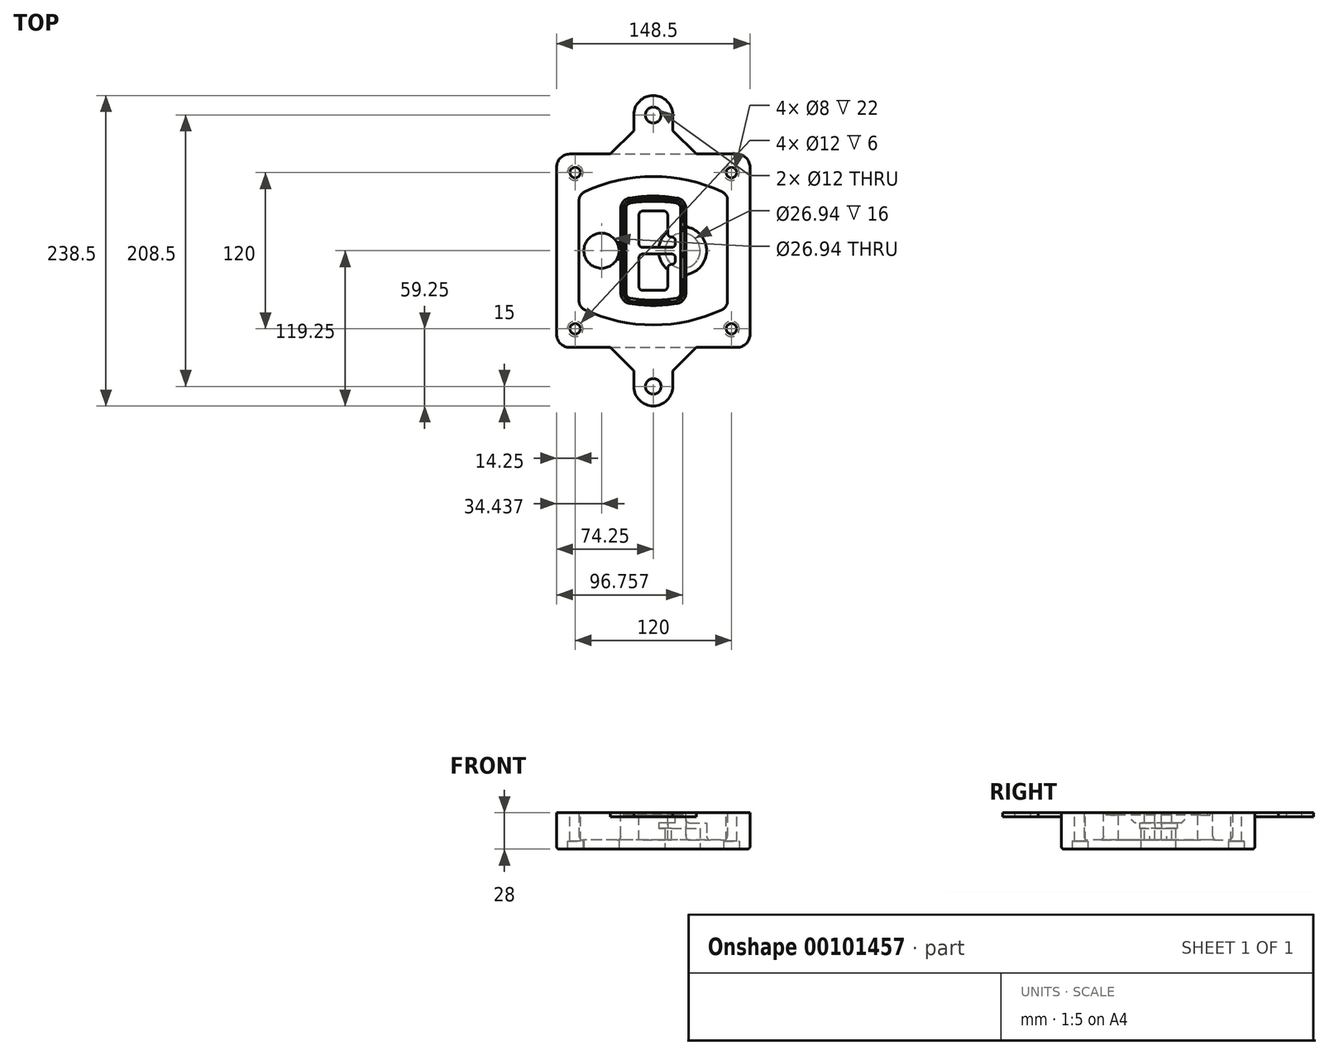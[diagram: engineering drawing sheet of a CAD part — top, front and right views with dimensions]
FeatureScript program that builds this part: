
annotation { "Feature Type Name" : "Feature", "Feature Type Description" : "" }
export const myFeature = defineFeature(function(context is Context, id is Id, definition is map)
    precondition{}
    {
        {
            var Q0;
            Q0=qCreatedBy(makeId("Top.planeOp"),FACE);
            var sketch = newSketch(context, id + "F0", { "sketchPlane" : qUnion([Q0])});
            skPoint(sketch, "E0.rect.middle", {"position": v(0, 0) * mm});
            skLineSegment(sketch, "E1.bottom", {"start": v(-64.25, -74.25) * mm, "end": v(64.25, -74.25) * mm});
            skLineSegment(sketch, "E1.top", {"start": v(-64.25, 74.25) * mm, "end": v(64.25, 74.25) * mm});
            skLineSegment(sketch, "E1.left", {"start": v(-74.25, -64.25) * mm, "end": v(-74.25, 64.25) * mm});
            skLineSegment(sketch, "E1.right", {"start": v(74.25, -64.25) * mm, "end": v(74.25, 64.25) * mm});
            skLineSegment(sketch, "E2", {"start": v(-74.25, 74.25) * mm, "end": v(74.25, -74.25) * mm, "construction": true});
            skLineSegment(sketch, "E3", {"start": v(74.25, 74.25) * mm, "end": v(-74.25, -74.25) * mm, "construction": true});
            skCircle(sketch, "E4", {"center": v(-60, 60) * mm, "radius": 4 * mm});
            skCircle(sketch, "E5", {"center": v(60, 60) * mm, "radius": 4 * mm});
            skCircle(sketch, "E6", {"center": v(60, -60) * mm, "radius": 4 * mm});
            skCircle(sketch, "E7", {"center": v(-60, -60) * mm, "radius": 4 * mm});
            skLineSegment(sketch, "E8", {"start": v(-60, 60) * mm, "end": v(60, 60) * mm, "construction": true});
            skLineSegment(sketch, "E9", {"start": v(60, 60) * mm, "end": v(60, -60) * mm, "construction": true});
            skLineSegment(sketch, "E10", {"start": v(60, -60) * mm, "end": v(-60, -60) * mm, "construction": true});
            skLineSegment(sketch, "E11", {"start": v(-60, -60) * mm, "end": v(-60, 60) * mm, "construction": true});
            skLineSegment(sketch, "E12", {"start": v(-60, 38.83) * mm, "end": v(-60, -38.83) * mm});
            skLineSegment(sketch, "E13", {"start": v(60, 38.83) * mm, "end": v(60, -38.83) * mm});
            skArc(sketch, "E14", {"start": v(54.26, 47.88) * mm, "mid": v(0, 60) * mm, "end": v(-54.26, 47.88) * mm});
            skArc(sketch, "E15", {"start": v(-54.26, -47.88) * mm, "mid": v(0, -60) * mm, "end": v(54.26, -47.88) * mm});
            skLineSegment(sketch, "E16", {"start": v(-60, 0) * mm, "end": v(60, 0) * mm, "construction": true});
            skPoint(sketch, "E17.visualSharp", {"position": v(-60, -45) * mm});
            skArc(sketch, "E17.filletArc", {"start": v(-60, -38.83) * mm, "mid": v(-58.44, -44.2) * mm, "end": v(-54.26, -47.88) * mm});
            skPoint(sketch, "E18.visualSharp", {"position": v(-60, 45) * mm});
            skArc(sketch, "E18.filletArc", {"start": v(-54.26, 47.88) * mm, "mid": v(-58.44, 44.2) * mm, "end": v(-60, 38.83) * mm});
            skPoint(sketch, "E19.visualSharp", {"position": v(60, 45) * mm});
            skArc(sketch, "E19.filletArc", {"start": v(60, 38.83) * mm, "mid": v(58.44, 44.2) * mm, "end": v(54.26, 47.88) * mm});
            skPoint(sketch, "E20.visualSharp", {"position": v(60, -45) * mm});
            skArc(sketch, "E20.filletArc", {"start": v(54.26, -47.88) * mm, "mid": v(58.44, -44.2) * mm, "end": v(60, -38.83) * mm});
            skPoint(sketch, "E21.visualSharp", {"position": v(-74.25, 74.25) * mm});
            skArc(sketch, "E21.filletArc", {"start": v(-64.25, 74.25) * mm, "mid": v(-71.32, 71.32) * mm, "end": v(-74.25, 64.25) * mm});
            skPoint(sketch, "E22.visualSharp", {"position": v(74.25, 74.25) * mm});
            skArc(sketch, "E22.filletArc", {"start": v(74.25, 64.25) * mm, "mid": v(71.32, 71.32) * mm, "end": v(64.25, 74.25) * mm});
            skPoint(sketch, "E23.visualSharp", {"position": v(74.25, -74.25) * mm});
            skArc(sketch, "E23.filletArc", {"start": v(64.25, -74.25) * mm, "mid": v(71.32, -71.32) * mm, "end": v(74.25, -64.25) * mm});
            skPoint(sketch, "E24.visualSharp", {"position": v(-74.25, -74.25) * mm});
            skArc(sketch, "E24.filletArc", {"start": v(-74.25, -64.25) * mm, "mid": v(-71.32, -71.32) * mm, "end": v(-64.25, -74.25) * mm});
            skArc(sketch, "E25.0", {"start": v(57, 38.83) * mm, "mid": v(55.9, 42.58) * mm, "end": v(52.98, 45.17) * mm});
            skLineSegment(sketch, "E25.1", {"start": v(57, 38.83) * mm, "end": v(57, -38.83) * mm});
            skArc(sketch, "E25.2", {"start": v(52.98, -45.17) * mm, "mid": v(55.9, -42.58) * mm, "end": v(57, -38.83) * mm});
            skArc(sketch, "E25.3", {"start": v(-52.98, -45.17) * mm, "mid": v(0, -57) * mm, "end": v(52.98, -45.17) * mm});
            skArc(sketch, "E25.4", {"start": v(-57, -38.83) * mm, "mid": v(-55.9, -42.58) * mm, "end": v(-52.98, -45.17) * mm});
            skArc(sketch, "E25.5", {"start": v(52.98, 45.17) * mm, "mid": v(0, 57) * mm, "end": v(-52.98, 45.17) * mm});
            skLineSegment(sketch, "E25.6", {"start": v(-57, 38.83) * mm, "end": v(-57, -38.83) * mm});
            skArc(sketch, "E25.7", {"start": v(-52.98, 45.17) * mm, "mid": v(-55.9, 42.58) * mm, "end": v(-57, 38.83) * mm});
            skArc(sketch, "E26.0", {"start": v(-55.96, 51.5) * mm, "mid": v(-61.82, 46.33) * mm, "end": v(-64, 38.83) * mm});
            skArc(sketch, "E26.1", {"start": v(55.96, 51.5) * mm, "mid": v(0, 64) * mm, "end": v(-55.96, 51.5) * mm});
            skArc(sketch, "E26.2", {"start": v(64, 38.83) * mm, "mid": v(61.82, 46.33) * mm, "end": v(55.96, 51.5) * mm});
            skLineSegment(sketch, "E26.3", {"start": v(64, 38.83) * mm, "end": v(64, -38.83) * mm});
            skArc(sketch, "E26.4", {"start": v(55.96, -51.5) * mm, "mid": v(61.82, -46.33) * mm, "end": v(64, -38.83) * mm});
            skLineSegment(sketch, "E26.5", {"start": v(-64, 38.83) * mm, "end": v(-64, -38.83) * mm});
            skArc(sketch, "E26.6", {"start": v(-55.96, -51.5) * mm, "mid": v(0, -64) * mm, "end": v(55.96, -51.5) * mm});
            skArc(sketch, "E26.7", {"start": v(-64, -38.83) * mm, "mid": v(-61.82, -46.33) * mm, "end": v(-55.96, -51.5) * mm});
            skSolve(sketch);
        }
        {
            var Q0;
            Q0=makeQuery(id+"F0.imprint","IMPRINT",FACE,{"disambiguationData":[TD([[makeQuery(id+"F0.imprint","IMPRINT",EDGE,{"derivedFrom":sQuery(id+"F0.wireOp",EDGE,"E1.bottom")}),1.0]])]});
            var Q1;
            Q1=makeQuery(id+"F0.imprint","IMPRINT",FACE,{"disambiguationData":[TD([[makeQuery(id+"F0.imprint","IMPRINT",EDGE,{"derivedFrom":sQuery(id+"F0.wireOp",EDGE,"E12")}),1.0]])]});
            var Q2;
            Q2=makeQuery(id+"F0.imprint","IMPRINT",FACE,{"disambiguationData":[TD([[makeQuery(id+"F0.imprint","IMPRINT",EDGE,{"derivedFrom":sQuery(id+"F0.wireOp",EDGE,"E25.0")}),1.0]])]});
            var Q3;
            Q3=makeQuery(id+"F0.imprint","IMPRINT",FACE,{"disambiguationData":[TD([[makeQuery(id+"F0.imprint","IMPRINT",EDGE,{"derivedFrom":sQuery(id+"F0.wireOp",EDGE,"E12")}),-1.0]])]});
            extrude(context, id + "F1", {"entities" : qUnion([Q0, Q1, Q2, Q3]), "oppositeDirection" : true, "depth" : 25 * mm});
        }
        {
            var Q0;
            Q0=makeQuery(id+"F0.imprint","IMPRINT",FACE,{"disambiguationData":[TD([[makeQuery(id+"F0.imprint","IMPRINT",EDGE,{"derivedFrom":sQuery(id+"F0.wireOp",EDGE,"E12")}),1.0]])]});
            extrude(context, id + "F2", {"entities" : qUnion([Q0]), "operationType" : NewBodyOperationType.ADD, "depth" : 3 * mm});
        }
        {
            var Q0;
            Q0=makeQuery(id+"F0.imprint","IMPRINT",FACE,{"disambiguationData":[TD([[makeQuery(id+"F0.imprint","IMPRINT",EDGE,{"derivedFrom":sQuery(id+"F0.wireOp",EDGE,"E25.0")}),1.0]])]});
            extrude(context, id + "F3", {"entities" : qUnion([Q0]), "operationType" : NewBodyOperationType.REMOVE, "oppositeDirection" : true, "depth" : 18 * mm});
        }
        {
            var Q0;
            Q0=makeQuery(id+"F2.opExtrude","CAP_FACE",FACE,{"disambiguationData":[OSD([sQuery(id+"F0.wireOp",EDGE,"E12"),sQuery(id+"F0.wireOp",EDGE,"E13"),sQuery(id+"F0.wireOp",EDGE,"E14"),sQuery(id+"F0.wireOp",EDGE,"E15"),sQuery(id+"F0.wireOp",EDGE,"E17.filletArc"),sQuery(id+"F0.wireOp",EDGE,"E18.filletArc"),sQuery(id+"F0.wireOp",EDGE,"E19.filletArc"),sQuery(id+"F0.wireOp",EDGE,"E20.filletArc"),sQuery(id+"F0.wireOp",EDGE,"E25.0"),sQuery(id+"F0.wireOp",EDGE,"E25.1"),sQuery(id+"F0.wireOp",EDGE,"E25.2"),sQuery(id+"F0.wireOp",EDGE,"E25.3"),sQuery(id+"F0.wireOp",EDGE,"E25.4"),sQuery(id+"F0.wireOp",EDGE,"E25.5"),sQuery(id+"F0.wireOp",EDGE,"E25.6"),sQuery(id+"F0.wireOp",EDGE,"E25.7")])],"isStart":false});
            var sketch = newSketch(context, id + "F4", { "sketchPlane" : qUnion([Q0])});
            skArc(sketch, "E27.0", {"start": v(-18.34, -40.45) * mm, "mid": v(0, -42) * mm, "end": v(18.34, -40.45) * mm});
            skArc(sketch, "E28.0", {"start": v(18.34, 40.45) * mm, "mid": v(0, 42) * mm, "end": v(-18.34, 40.45) * mm});
            skLineSegment(sketch, "E29", {"start": v(-25, 32.57) * mm, "end": v(-25, -32.57) * mm});
            skLineSegment(sketch, "E30", {"start": v(25, 32.57) * mm, "end": v(25, -32.57) * mm});
            skLineSegment(sketch, "E31", {"start": v(-25, 39.1) * mm, "end": v(25, 39.1) * mm, "construction": true});
            skLineSegment(sketch, "E32", {"start": v(-25, -39.1) * mm, "end": v(25, -39.1) * mm, "construction": true});
            skPoint(sketch, "E33.visualSharp", {"position": v(-25, 39.1) * mm});
            skArc(sketch, "E33.filletArc", {"start": v(-18.34, 40.45) * mm, "mid": v(-23.11, 37.73) * mm, "end": v(-25, 32.57) * mm});
            skPoint(sketch, "E34.visualSharp", {"position": v(25, 39.1) * mm});
            skArc(sketch, "E34.filletArc", {"start": v(25, 32.57) * mm, "mid": v(23.11, 37.73) * mm, "end": v(18.34, 40.45) * mm});
            skPoint(sketch, "E35.visualSharp", {"position": v(25, -39.1) * mm});
            skArc(sketch, "E35.filletArc", {"start": v(18.34, -40.45) * mm, "mid": v(23.11, -37.73) * mm, "end": v(25, -32.57) * mm});
            skPoint(sketch, "E36.visualSharp", {"position": v(-25, -39.1) * mm});
            skArc(sketch, "E36.filletArc", {"start": v(-25, -32.57) * mm, "mid": v(-23.11, -37.73) * mm, "end": v(-18.34, -40.45) * mm});
            skArc(sketch, "E37.0", {"start": v(52.98, 45.17) * mm, "mid": v(0, 57) * mm, "end": v(-52.98, 45.17) * mm});
            skArc(sketch, "E37.1", {"start": v(-52.98, 45.17) * mm, "mid": v(-55.9, 42.58) * mm, "end": v(-57, 38.83) * mm});
            skLineSegment(sketch, "E37.2", {"start": v(-57, 38.83) * mm, "end": v(-57, -38.83) * mm});
            skArc(sketch, "E37.3", {"start": v(-57, -38.83) * mm, "mid": v(-55.9, -42.58) * mm, "end": v(-52.98, -45.17) * mm});
            skArc(sketch, "E37.4", {"start": v(-52.98, -45.17) * mm, "mid": v(0, -57) * mm, "end": v(52.98, -45.17) * mm});
            skArc(sketch, "E37.5", {"start": v(52.98, -45.17) * mm, "mid": v(55.9, -42.58) * mm, "end": v(57, -38.83) * mm});
            skLineSegment(sketch, "E37.6", {"start": v(57, 38.83) * mm, "end": v(57, -38.83) * mm});
            skArc(sketch, "E37.7", {"start": v(57, 38.83) * mm, "mid": v(55.9, 42.58) * mm, "end": v(52.98, 45.17) * mm});
            skLineSegment(sketch, "E38.0", {"start": v(23, 32.57) * mm, "end": v(23, -32.57) * mm});
            skArc(sketch, "E38.1", {"start": v(18, -38.48) * mm, "mid": v(21.58, -36.44) * mm, "end": v(23, -32.57) * mm});
            skArc(sketch, "E38.2", {"start": v(-18, -38.48) * mm, "mid": v(0, -40) * mm, "end": v(18, -38.48) * mm});
            skArc(sketch, "E38.3", {"start": v(-23, -32.57) * mm, "mid": v(-21.58, -36.44) * mm, "end": v(-18, -38.48) * mm});
            skLineSegment(sketch, "E38.4", {"start": v(-23, 32.57) * mm, "end": v(-23, -32.57) * mm});
            skArc(sketch, "E38.5", {"start": v(23, 32.57) * mm, "mid": v(21.58, 36.44) * mm, "end": v(18, 38.48) * mm});
            skArc(sketch, "E38.6", {"start": v(-18, 38.48) * mm, "mid": v(-21.58, 36.44) * mm, "end": v(-23, 32.57) * mm});
            skArc(sketch, "E38.7", {"start": v(18, 38.48) * mm, "mid": v(0, 40) * mm, "end": v(-18, 38.48) * mm});
            skArc(sketch, "E39.0", {"start": v(21, 32.57) * mm, "mid": v(20.06, 35.15) * mm, "end": v(17.67, 36.5) * mm});
            skLineSegment(sketch, "E39.1", {"start": v(21, 32.57) * mm, "end": v(21, -32.57) * mm});
            skArc(sketch, "E39.2", {"start": v(17.67, -36.5) * mm, "mid": v(20.06, -35.15) * mm, "end": v(21, -32.57) * mm});
            skArc(sketch, "E39.3", {"start": v(-17.67, -36.5) * mm, "mid": v(0, -38) * mm, "end": v(17.67, -36.5) * mm});
            skArc(sketch, "E39.4", {"start": v(-21, -32.57) * mm, "mid": v(-20.06, -35.15) * mm, "end": v(-17.67, -36.5) * mm});
            skArc(sketch, "E39.5", {"start": v(17.67, 36.5) * mm, "mid": v(0, 38) * mm, "end": v(-17.67, 36.5) * mm});
            skLineSegment(sketch, "E39.6", {"start": v(-21, 32.57) * mm, "end": v(-21, -32.57) * mm});
            skArc(sketch, "E39.7", {"start": v(-17.67, 36.5) * mm, "mid": v(-20.06, 35.15) * mm, "end": v(-21, 32.57) * mm});
            skLineSegment(sketch, "E40", {"start": v(-25, 0) * mm, "end": v(25, 0) * mm, "construction": true});
            skLineSegment(sketch, "E41", {"start": v(-11, 5.5) * mm, "end": v(-11, 27.5) * mm});
            skLineSegment(sketch, "E42", {"start": v(-8, 30.5) * mm, "end": v(8, 30.5) * mm});
            skLineSegment(sketch, "E43", {"start": v(11, 27.5) * mm, "end": v(11, 13.5) * mm});
            skLineSegment(sketch, "E44", {"start": v(14, 10.5) * mm, "end": v(14, 10.5) * mm});
            skLineSegment(sketch, "E45", {"start": v(17, 7.5) * mm, "end": v(17, 5.5) * mm});
            skLineSegment(sketch, "E46", {"start": v(14, 2.5) * mm, "end": v(-8, 2.5) * mm});
            skPoint(sketch, "E47.visualSharp", {"position": v(-11, 30.5) * mm});
            skArc(sketch, "E47.filletArc", {"start": v(-8, 30.5) * mm, "mid": v(-10.12, 29.62) * mm, "end": v(-11, 27.5) * mm});
            skPoint(sketch, "E48.visualSharp", {"position": v(11, 30.5) * mm});
            skArc(sketch, "E48.filletArc", {"start": v(11, 27.5) * mm, "mid": v(10.12, 29.62) * mm, "end": v(8, 30.5) * mm});
            skPoint(sketch, "E49.visualSharp", {"position": v(11, 10.5) * mm});
            skArc(sketch, "E49.filletArc", {"start": v(11, 13.5) * mm, "mid": v(11.88, 11.38) * mm, "end": v(14, 10.5) * mm});
            skPoint(sketch, "E50.visualSharp", {"position": v(17, 10.5) * mm});
            skArc(sketch, "E50.filletArc", {"start": v(17, 7.5) * mm, "mid": v(16.12, 9.62) * mm, "end": v(14, 10.5) * mm});
            skPoint(sketch, "E51.visualSharp", {"position": v(17, 2.5) * mm});
            skArc(sketch, "E51.filletArc", {"start": v(14, 2.5) * mm, "mid": v(16.12, 3.38) * mm, "end": v(17, 5.5) * mm});
            skPoint(sketch, "E52.visualSharp", {"position": v(-11, 2.5) * mm});
            skArc(sketch, "E52.filletArc", {"start": v(-11, 5.5) * mm, "mid": v(-10.12, 3.38) * mm, "end": v(-8, 2.5) * mm});
            skLineSegment(sketch, "E53.0.MirrorCS", {"start": v(14, -2.5) * mm, "end": v(-8, -2.5) * mm});
            skArc(sketch, "E54.0.MirrorCS", {"start": v(-11, -5.5) * mm, "mid": v(-10.12, -3.38) * mm, "end": v(-8, -2.5) * mm});
            skLineSegment(sketch, "E55.0.MirrorCS", {"start": v(-11, -5.5) * mm, "end": v(-11, -27.5) * mm});
            skArc(sketch, "E56.0.MirrorCS", {"start": v(-8, -30.5) * mm, "mid": v(-10.12, -29.62) * mm, "end": v(-11, -27.5) * mm});
            skLineSegment(sketch, "E57.0.MirrorCS", {"start": v(-8, -30.5) * mm, "end": v(8, -30.5) * mm});
            skArc(sketch, "E58.0.MirrorCS", {"start": v(11, -27.5) * mm, "mid": v(10.12, -29.62) * mm, "end": v(8, -30.5) * mm});
            skLineSegment(sketch, "E59.0.MirrorCS", {"start": v(11, -27.5) * mm, "end": v(11, -13.5) * mm});
            skArc(sketch, "E60.0.MirrorCS", {"start": v(11, -13.5) * mm, "mid": v(11.88, -11.38) * mm, "end": v(14, -10.5) * mm});
            skArc(sketch, "E61.0.MirrorCS", {"start": v(17, -7.5) * mm, "mid": v(16.12, -9.62) * mm, "end": v(14, -10.5) * mm});
            skLineSegment(sketch, "E62.0.MirrorCS", {"start": v(17, -7.5) * mm, "end": v(17, -5.5) * mm});
            skArc(sketch, "E63.0.MirrorCS", {"start": v(14, -2.5) * mm, "mid": v(16.12, -3.38) * mm, "end": v(17, -5.5) * mm});
            skSolve(sketch);
        }
        {
            var Q0;
            Q0=makeQuery(id+"F4.imprint","IMPRINT",FACE,{"disambiguationData":[TD([[makeQuery(id+"F4.imprint","IMPRINT",EDGE,{"derivedFrom":sQuery(id+"F4.wireOp",EDGE,"E27.0")}),1.0]])]});
            var Q1;
            Q1=makeQuery(id+"F4.imprint","IMPRINT",FACE,{"disambiguationData":[TD([[makeQuery(id+"F4.imprint","IMPRINT",EDGE,{"derivedFrom":sQuery(id+"F4.wireOp",EDGE,"E38.0")}),-1.0]])]});
            var Q2;
            Q2=makeQuery(id+"F4.imprint","IMPRINT",FACE,{"disambiguationData":[TD([[makeQuery(id+"F4.imprint","IMPRINT",EDGE,{"derivedFrom":sQuery(id+"F4.wireOp",EDGE,"E39.0")}),1.0]])]});
            extrude(context, id + "F5", {"entities" : qUnion([Q0, Q1, Q2]), "operationType" : NewBodyOperationType.ADD, "endBound" : BoundingType.UP_TO_NEXT, "oppositeDirection" : true, "depth" : 25 * mm});
        }
        {
            var Q0;
            Q0=makeQuery(id+"F4.imprint","IMPRINT",FACE,{"disambiguationData":[TD([[makeQuery(id+"F4.imprint","IMPRINT",EDGE,{"derivedFrom":sQuery(id+"F4.wireOp",EDGE,"E38.0")}),-1.0]])]});
            extrude(context, id + "F6", {"entities" : qUnion([Q0]), "operationType" : NewBodyOperationType.REMOVE, "oppositeDirection" : true, "depth" : 2 * mm});
        }
        {
            var Q0;
            Q0=makeQuery(id+"F1.opExtrude","CAP_FACE",FACE,{"disambiguationData":[OSD([sQuery(id+"F0.wireOp",EDGE,"E1.bottom"),sQuery(id+"F0.wireOp",EDGE,"E1.top"),sQuery(id+"F0.wireOp",EDGE,"E1.left"),sQuery(id+"F0.wireOp",EDGE,"E1.right"),sQuery(id+"F0.wireOp",EDGE,"E4"),sQuery(id+"F0.wireOp",EDGE,"E5"),sQuery(id+"F0.wireOp",EDGE,"E6"),sQuery(id+"F0.wireOp",EDGE,"E7"),sQuery(id+"F0.wireOp",EDGE,"E21.filletArc"),sQuery(id+"F0.wireOp",EDGE,"E22.filletArc"),sQuery(id+"F0.wireOp",EDGE,"E23.filletArc"),sQuery(id+"F0.wireOp",EDGE,"E24.filletArc")])],"isStart":false});
            var sketch = newSketch(context, id + "F7", { "sketchPlane" : qUnion([Q0])});
            skCircle(sketch, "E64", {"center": v(22.5, 0) * mm, "radius": 13.47 * mm});
            skCircle(sketch, "E65", {"center": v(-39.81, 0) * mm, "radius": 13.47 * mm});
            skLineSegment(sketch, "E66", {"start": v(74.25, 0) * mm, "end": v(-74.25, 0) * mm});
            skCircle(sketch, "E67", {"center": v(22.5, 0) * mm, "radius": 18.47 * mm});
            skCircle(sketch, "E68", {"center": v(60, -60) * mm, "radius": 6 * mm});
            skCircle(sketch, "E69", {"center": v(-60, -60) * mm, "radius": 6 * mm});
            skCircle(sketch, "E70", {"center": v(-60, 60) * mm, "radius": 6 * mm});
            skCircle(sketch, "E71", {"center": v(60, 60) * mm, "radius": 6 * mm});
            skSolve(sketch);
        }
        {
            var Q0;
            {var subQ1=sQuery(id+"F7.wireOp",EDGE,"E66");var subQ4=sQuery(id+"F7.wireOp",EDGE,"E64");var subQ6=makeQuery(id+"F7.imprint","INTERSECT",VERTEX,{"disambiguationData":[OD(0.0)],"derivedFrom":[subQ4,subQ1]});Q0=makeQuery(id+"F7.imprint","IMPRINT",FACE,{"disambiguationData":[TD([[makeQuery(id+"F7.imprint","IMPRINT",EDGE,{"disambiguationData":[TD([[subQ6,-1.0]])],"derivedFrom":subQ4}),-1.0]])]});}
            var Q1;
            {var subQ0=sQuery(id+"F7.wireOp",EDGE,"E66");var subQ1=sQuery(id+"F7.wireOp",EDGE,"E64");var subQ3=makeQuery(id+"F7.imprint","INTERSECT",VERTEX,{"disambiguationData":[OD(0.0)],"derivedFrom":[subQ1,subQ0]});Q1=makeQuery(id+"F7.imprint","IMPRINT",FACE,{"disambiguationData":[TD([[makeQuery(id+"F7.imprint","IMPRINT",EDGE,{"disambiguationData":[TD([[subQ3,-1.0]])],"derivedFrom":subQ1}),1.0]])]});}
            var Q2;
            {var subQ0=sQuery(id+"F7.wireOp",EDGE,"E66");var subQ1=sQuery(id+"F7.wireOp",EDGE,"E64");var subQ3=makeQuery(id+"F7.imprint","INTERSECT",VERTEX,{"disambiguationData":[OD(0.0)],"derivedFrom":[subQ1,subQ0]});Q2=makeQuery(id+"F7.imprint","IMPRINT",FACE,{"disambiguationData":[TD([[makeQuery(id+"F7.imprint","IMPRINT",EDGE,{"disambiguationData":[TD([[subQ3,1.0]])],"derivedFrom":subQ1}),1.0]])]});}
            var Q3;
            {var subQ1=sQuery(id+"F7.wireOp",EDGE,"E66");var subQ4=sQuery(id+"F7.wireOp",EDGE,"E64");var subQ6=makeQuery(id+"F7.imprint","INTERSECT",VERTEX,{"disambiguationData":[OD(0.0)],"derivedFrom":[subQ4,subQ1]});Q3=makeQuery(id+"F7.imprint","IMPRINT",FACE,{"disambiguationData":[TD([[makeQuery(id+"F7.imprint","IMPRINT",EDGE,{"disambiguationData":[TD([[subQ6,1.0]])],"derivedFrom":subQ4}),-1.0]])]});}
            extrude(context, id + "F8", {"entities" : qUnion([Q0, Q1, Q2, Q3]), "operationType" : NewBodyOperationType.ADD, "oppositeDirection" : true, "depth" : 20 * mm});
        }
        {
            var Q0;
            {var subQ0=sQuery(id+"F7.wireOp",EDGE,"E66");var subQ1=sQuery(id+"F7.wireOp",EDGE,"E64");var subQ3=makeQuery(id+"F7.imprint","INTERSECT",VERTEX,{"disambiguationData":[OD(0.0)],"derivedFrom":[subQ1,subQ0]});Q0=makeQuery(id+"F7.imprint","IMPRINT",FACE,{"disambiguationData":[TD([[makeQuery(id+"F7.imprint","IMPRINT",EDGE,{"disambiguationData":[TD([[subQ3,-1.0]])],"derivedFrom":subQ1}),1.0]])]});}
            var Q1;
            {var subQ0=sQuery(id+"F7.wireOp",EDGE,"E66");var subQ1=sQuery(id+"F7.wireOp",EDGE,"E64");var subQ3=makeQuery(id+"F7.imprint","INTERSECT",VERTEX,{"disambiguationData":[OD(0.0)],"derivedFrom":[subQ1,subQ0]});Q1=makeQuery(id+"F7.imprint","IMPRINT",FACE,{"disambiguationData":[TD([[makeQuery(id+"F7.imprint","IMPRINT",EDGE,{"disambiguationData":[TD([[subQ3,1.0]])],"derivedFrom":subQ1}),1.0]])]});}
            extrude(context, id + "F9", {"entities" : qUnion([Q0, Q1]), "operationType" : NewBodyOperationType.REMOVE, "oppositeDirection" : true, "depth" : 16 * mm});
        }
        {
            var Q0;
            {var subQ0=sQuery(id+"F7.wireOp",EDGE,"E66");var subQ1=sQuery(id+"F7.wireOp",EDGE,"E65");var subQ3=makeQuery(id+"F7.imprint","INTERSECT",VERTEX,{"disambiguationData":[OD(0.0)],"derivedFrom":[subQ1,subQ0]});Q0=makeQuery(id+"F7.imprint","IMPRINT",FACE,{"disambiguationData":[TD([[makeQuery(id+"F7.imprint","IMPRINT",EDGE,{"disambiguationData":[TD([[subQ3,-1.0]])],"derivedFrom":subQ1}),1.0]])]});}
            var Q1;
            {var subQ0=sQuery(id+"F7.wireOp",EDGE,"E66");var subQ1=sQuery(id+"F7.wireOp",EDGE,"E65");var subQ3=makeQuery(id+"F7.imprint","INTERSECT",VERTEX,{"disambiguationData":[OD(0.0)],"derivedFrom":[subQ1,subQ0]});Q1=makeQuery(id+"F7.imprint","IMPRINT",FACE,{"disambiguationData":[TD([[makeQuery(id+"F7.imprint","IMPRINT",EDGE,{"disambiguationData":[TD([[subQ3,1.0]])],"derivedFrom":subQ1}),1.0]])]});}
            extrude(context, id + "F10", {"entities" : qUnion([Q0, Q1]), "operationType" : NewBodyOperationType.REMOVE, "oppositeDirection" : true, "depth" : 25 * mm});
        }
        {
            var Q0;
            Q0=makeQuery(id+"F7.imprint","IMPRINT",FACE,{"disambiguationData":[TD([[makeQuery(id+"F7.imprint","IMPRINT",EDGE,{"derivedFrom":sQuery(id+"F7.wireOp",EDGE,"E68")}),1.0]])]});
            var Q1;
            Q1=makeQuery(id+"F7.imprint","IMPRINT",FACE,{"disambiguationData":[TD([[makeQuery(id+"F7.imprint","IMPRINT",EDGE,{"derivedFrom":makeQuery(id+"F1.opExtrude","CAP_EDGE",EDGE,{"disambiguationData":[OSD([sQuery(id+"F0.wireOp",EDGE,"E5")])],"isStart":false})}),-1.0]])]});
            var Q2;
            Q2=makeQuery(id+"F7.imprint","IMPRINT",FACE,{"disambiguationData":[TD([[makeQuery(id+"F7.imprint","IMPRINT",EDGE,{"derivedFrom":sQuery(id+"F7.wireOp",EDGE,"E69")}),1.0]])]});
            var Q3;
            Q3=makeQuery(id+"F7.imprint","IMPRINT",FACE,{"disambiguationData":[TD([[makeQuery(id+"F7.imprint","IMPRINT",EDGE,{"derivedFrom":makeQuery(id+"F1.opExtrude","CAP_EDGE",EDGE,{"disambiguationData":[OSD([sQuery(id+"F0.wireOp",EDGE,"E4")])],"isStart":false})}),-1.0]])]});
            var Q4;
            Q4=makeQuery(id+"F7.imprint","IMPRINT",FACE,{"disambiguationData":[TD([[makeQuery(id+"F7.imprint","IMPRINT",EDGE,{"derivedFrom":sQuery(id+"F7.wireOp",EDGE,"E70")}),1.0]])]});
            var Q5;
            Q5=makeQuery(id+"F7.imprint","IMPRINT",FACE,{"disambiguationData":[TD([[makeQuery(id+"F7.imprint","IMPRINT",EDGE,{"derivedFrom":makeQuery(id+"F1.opExtrude","CAP_EDGE",EDGE,{"disambiguationData":[OSD([sQuery(id+"F0.wireOp",EDGE,"E7")])],"isStart":false})}),-1.0]])]});
            var Q6;
            Q6=makeQuery(id+"F7.imprint","IMPRINT",FACE,{"disambiguationData":[TD([[makeQuery(id+"F7.imprint","IMPRINT",EDGE,{"derivedFrom":sQuery(id+"F7.wireOp",EDGE,"E71")}),1.0]])]});
            var Q7;
            Q7=makeQuery(id+"F7.imprint","IMPRINT",FACE,{"disambiguationData":[TD([[makeQuery(id+"F7.imprint","IMPRINT",EDGE,{"derivedFrom":makeQuery(id+"F1.opExtrude","CAP_EDGE",EDGE,{"disambiguationData":[OSD([sQuery(id+"F0.wireOp",EDGE,"E6")])],"isStart":false})}),-1.0]])]});
            extrude(context, id + "F11", {"entities" : qUnion([Q0, Q1, Q2, Q3, Q4, Q5, Q6, Q7]), "operationType" : NewBodyOperationType.REMOVE, "oppositeDirection" : true, "depth" : 6 * mm});
        }
        {
            var Q0;
            Q0=makeQuery(id+"F9.boolean.opBoolean","COPY",FACE,{"derivedFrom":makeQuery(id+"F9.opExtrude","CAP_FACE",FACE,{"disambiguationData":[OSD([sQuery(id+"F7.wireOp",EDGE,"E64")])],"isStart":false})});
            var sketch = newSketch(context, id + "F12", { "sketchPlane" : qUnion([Q0])});
            skArc(sketch, "E72.0", {"start": v(11, 14.45) * mm, "mid": v(6.45, 9.13) * mm, "end": v(4.2, 2.5) * mm});
            skArc(sketch, "E72.1", {"start": v(4.2, -2.5) * mm, "mid": v(6.45, -9.13) * mm, "end": v(11, -14.45) * mm});
            skLineSegment(sketch, "E73", {"start": v(4.2, -2.5) * mm, "end": v(14, -2.5) * mm});
            skLineSegment(sketch, "E74.0", {"start": v(14, 2.5) * mm, "end": v(4.2, 2.5) * mm});
            skArc(sketch, "E74.1", {"start": v(14, 2.5) * mm, "mid": v(16.12, 3.38) * mm, "end": v(17, 5.5) * mm});
            skLineSegment(sketch, "E74.2", {"start": v(17, 7.5) * mm, "end": v(17, 5.5) * mm});
            skArc(sketch, "E74.3", {"start": v(17, 7.5) * mm, "mid": v(16.12, 9.62) * mm, "end": v(14, 10.5) * mm});
            skArc(sketch, "E74.4", {"start": v(11, 13.5) * mm, "mid": v(11.88, 11.38) * mm, "end": v(14, 10.5) * mm});
            skLineSegment(sketch, "E74.5", {"start": v(11, 14.45) * mm, "end": v(11, 13.5) * mm});
            skLineSegment(sketch, "E74.7", {"start": v(14, -2.5) * mm, "end": v(4.2, -2.5) * mm});
            skArc(sketch, "E74.8", {"start": v(14, -2.5) * mm, "mid": v(16.12, -3.38) * mm, "end": v(17, -5.5) * mm});
            skLineSegment(sketch, "E74.9", {"start": v(17, -7.5) * mm, "end": v(17, -5.5) * mm});
            skArc(sketch, "E74.10", {"start": v(17, -7.5) * mm, "mid": v(16.12, -9.62) * mm, "end": v(14, -10.5) * mm});
            skArc(sketch, "E74.11", {"start": v(11, -13.5) * mm, "mid": v(11.88, -11.38) * mm, "end": v(14, -10.5) * mm});
            skLineSegment(sketch, "E74.12", {"start": v(11, -14.45) * mm, "end": v(11, -13.5) * mm});
            skPoint(sketch, "E75.orphan", {"position": v(11, -27.5) * mm});
            skPoint(sketch, "E76.orphan", {"position": v(-8, -2.5) * mm});
            skPoint(sketch, "E77.orphan", {"position": v(-8, 2.5) * mm});
            skPoint(sketch, "E78.orphan", {"position": v(11, 27.5) * mm});
            skSolve(sketch);
        }
        {
            var Q0;
            {var subQ7=sQuery(id+"F12.wireOp",EDGE,"E72.0");var subQ14=sQuery(id+"F12.wireOp",EDGE,"E72.1");var subQ16=sQuery(id+"F12.wireOp",EDGE,"E74.1");var subQ18=sQuery(id+"F12.wireOp",EDGE,"E74.8");Q0=qUnion([makeQuery(id+"F12.imprint","IMPRINT",FACE,{"disambiguationData":[TD([[makeQuery(id+"F12.imprint","IMPRINT",EDGE,{"derivedFrom":subQ7}),1.0]])]}),makeQuery(id+"F12.imprint","IMPRINT",FACE,{"disambiguationData":[TD([[makeQuery(id+"F12.imprint","IMPRINT",EDGE,{"derivedFrom":subQ14}),1.0]])]}),makeQuery(id+"F12.imprint","IMPRINT",FACE,{"disambiguationData":[TD([[makeQuery(id+"F12.imprint","IMPRINT",EDGE,{"derivedFrom":subQ16}),1.0]])]}),makeQuery(id+"F12.imprint","IMPRINT",FACE,{"disambiguationData":[TD([[makeQuery(id+"F12.imprint","IMPRINT",EDGE,{"derivedFrom":subQ18}),-1.0]])]})]);}
            var Q1;
            Q1=makeQuery(id+"F5.boolean.opBoolean","SPLIT",FACE,{"disambiguationData":[TD([makeQuery(id+"F5.opExtrude","SWEPT_FACE",FACE,{"disambiguationData":[OSD([sQuery(id+"F4.wireOp",EDGE,"E41")])]})])],"derivedFrom":makeQuery(id+"F3.boolean.opBoolean","COPY",FACE,{"derivedFrom":makeQuery(id+"F3.opExtrude","CAP_FACE",FACE,{"disambiguationData":[OSD([sQuery(id+"F0.wireOp",EDGE,"E25.0"),sQuery(id+"F0.wireOp",EDGE,"E25.1"),sQuery(id+"F0.wireOp",EDGE,"E25.2"),sQuery(id+"F0.wireOp",EDGE,"E25.3"),sQuery(id+"F0.wireOp",EDGE,"E25.4"),sQuery(id+"F0.wireOp",EDGE,"E25.5"),sQuery(id+"F0.wireOp",EDGE,"E25.6"),sQuery(id+"F0.wireOp",EDGE,"E25.7")])],"isStart":false})})});
            extrude(context, id + "F13", {"entities" : qUnion([Q0]), "operationType" : NewBodyOperationType.REMOVE, "endBound" : BoundingType.UP_TO_SURFACE, "endBoundEntityFace" : qUnion([Q1]), "depth" : 25 * mm});
        }
        {
            var Q0;
            Q0=makeQuery(id+"F3.boolean.opBoolean","COPY",EDGE,{"derivedFrom":makeQuery(id+"F3.opExtrude","CAP_EDGE",EDGE,{"disambiguationData":[OSD([sQuery(id+"F0.wireOp",EDGE,"E25.6")])],"isStart":false})});
            var Q1;
            Q1=makeQuery(id+"F8.boolean.opBoolean","INTERSECT",EDGE,{"derivedFrom":[makeQuery(id+"F5.opExtrude","SWEPT_FACE",FACE,{"disambiguationData":[OSD([sQuery(id+"F4.wireOp",EDGE,"E30")])]}),makeQuery(id+"F8.opExtrude","CAP_FACE",FACE,{"disambiguationData":[OSD([sQuery(id+"F7.wireOp",EDGE,"E67")])],"isStart":false})]});
            var Q2;
            Q2=makeQuery(id+"F8.boolean.opBoolean","INTERSECT",EDGE,{"disambiguationData":[OD(1.0)],"derivedFrom":[makeQuery(id+"F5.opExtrude","SWEPT_FACE",FACE,{"disambiguationData":[OSD([sQuery(id+"F4.wireOp",EDGE,"E30")])]}),makeQuery(id+"F8.opExtrude","SWEPT_FACE",FACE,{"disambiguationData":[OSD([sQuery(id+"F7.wireOp",EDGE,"E67")])]})]});
            var Q3;
            {var subQ0=sQuery(id+"F4.wireOp",EDGE,"E30");Q3=makeQuery(id+"F8.boolean.opBoolean","SPLIT",EDGE,{"disambiguationData":[TD([makeQuery(id+"F5.opExtrude","SWEPT_FACE",FACE,{"disambiguationData":[OSD([sQuery(id+"F4.wireOp",EDGE,"E35.filletArc")])]})])],"derivedFrom":makeQuery(id+"F5.opExtrude","CAP_EDGE",EDGE,{"disambiguationData":[OSD([subQ0])],"isStart":false})});}
            var Q4;
            {var subQ0=sQuery(id+"F0.wireOp",EDGE,"E25.7");var subQ1=sQuery(id+"F0.wireOp",EDGE,"E25.1");var subQ2=sQuery(id+"F0.wireOp",EDGE,"E25.6");var subQ3=sQuery(id+"F0.wireOp",EDGE,"E25.5");var subQ4=sQuery(id+"F0.wireOp",EDGE,"E25.4");var subQ5=sQuery(id+"F0.wireOp",EDGE,"E25.0");var subQ6=sQuery(id+"F0.wireOp",EDGE,"E25.2");var subQ7=sQuery(id+"F0.wireOp",EDGE,"E25.3");Q4=makeQuery(id+"F8.boolean.opBoolean","INTERSECT",EDGE,{"derivedFrom":[makeQuery(id+"F5.boolean.opBoolean","SPLIT",FACE,{"disambiguationData":[TD([makeQuery(id+"F2.opExtrude","SWEPT_FACE",FACE,{"disambiguationData":[OSD([subQ5])]})])],"derivedFrom":makeQuery(id+"F3.boolean.opBoolean","COPY",FACE,{"derivedFrom":makeQuery(id+"F3.opExtrude","CAP_FACE",FACE,{"disambiguationData":[OSD([subQ5,subQ1,subQ6,subQ7,subQ4,subQ3,subQ2,subQ0])],"isStart":false})})}),makeQuery(id+"F8.opExtrude","SWEPT_FACE",FACE,{"disambiguationData":[OSD([sQuery(id+"F7.wireOp",EDGE,"E67")])]})]});}
            var Q5;
            Q5=makeQuery(id+"F8.boolean.opBoolean","INTERSECT",EDGE,{"disambiguationData":[OD(0.0)],"derivedFrom":[makeQuery(id+"F5.opExtrude","SWEPT_FACE",FACE,{"disambiguationData":[OSD([sQuery(id+"F4.wireOp",EDGE,"E30")])]}),makeQuery(id+"F8.opExtrude","SWEPT_FACE",FACE,{"disambiguationData":[OSD([sQuery(id+"F7.wireOp",EDGE,"E67")])]})]});
            fillet(context, id + "F14", {"entities" : qUnion([Q0, Q1, Q2, Q3, Q4, Q5]), "radius" : 3 * mm, "tangentPropagation" : true, "allowEdgeOverflow" : false});
        }
        {
            var Q0;
            Q0=makeQuery(id+"F1.opExtrude","CAP_EDGE",EDGE,{"disambiguationData":[OSD([sQuery(id+"F0.wireOp",EDGE,"E1.bottom")])],"isStart":false});
            fillet(context, id + "F15", {"entities" : qUnion([Q0]), "radius" : 2 * mm, "tangentPropagation" : true, "allowEdgeOverflow" : false});
        }
        {
            var Q0;
            {var subQ0=sQuery(id+"F0.wireOp",EDGE,"E22.filletArc");var subQ1=sQuery(id+"F0.wireOp",EDGE,"E7");var subQ2=sQuery(id+"F0.wireOp",EDGE,"E6");var subQ3=sQuery(id+"F0.wireOp",EDGE,"E5");var subQ4=sQuery(id+"F0.wireOp",EDGE,"E4");var subQ5=sQuery(id+"F0.wireOp",EDGE,"E1.bottom");var subQ6=sQuery(id+"F0.wireOp",EDGE,"E21.filletArc");var subQ7=sQuery(id+"F0.wireOp",EDGE,"E1.top");var subQ8=sQuery(id+"F0.wireOp",EDGE,"E1.left");var subQ9=sQuery(id+"F0.wireOp",EDGE,"E1.right");var subQ10=sQuery(id+"F0.wireOp",EDGE,"E23.filletArc");var subQ11=sQuery(id+"F0.wireOp",EDGE,"E24.filletArc");Q0=makeQuery(id+"F2.boolean.opBoolean","SPLIT",FACE,{"disambiguationData":[TD([makeQuery(id+"F1.opExtrude","SWEPT_FACE",FACE,{"disambiguationData":[OSD([subQ5])]})])],"derivedFrom":makeQuery(id+"F1.opExtrude","CAP_FACE",FACE,{"disambiguationData":[OSD([subQ5,subQ7,subQ8,subQ9,subQ4,subQ3,subQ2,subQ1,subQ6,subQ0,subQ10,subQ11])],"isStart":true})});}
            var sketch = newSketch(context, id + "F16", { "sketchPlane" : qUnion([Q0])});
            skLineSegment(sketch, "E79", {"start": v(0, 74.25) * mm, "end": v(0, 104.25) * mm});
            skCircle(sketch, "E80", {"center": v(0, 104.25) * mm, "radius": 6 * mm});
            skLineSegment(sketch, "E81", {"start": v(-33, 74.25) * mm, "end": v(-15, 92.25) * mm});
            skLineSegment(sketch, "E82", {"start": v(-15, 92.25) * mm, "end": v(-15, 104.3) * mm});
            skArc(sketch, "E83", {"start": v(15, 104.3) * mm, "mid": v(0, 119.25) * mm, "end": v(-15, 104.3) * mm});
            skLineSegment(sketch, "E84", {"start": v(15, 104.3) * mm, "end": v(15, 92.25) * mm});
            skLineSegment(sketch, "E85", {"start": v(15, 92.25) * mm, "end": v(33, 74.25) * mm});
            skLineSegment(sketch, "E86", {"start": v(-74.25, 0) * mm, "end": v(74.25, 0) * mm, "construction": true});
            skLineSegment(sketch, "E87.MirrorCS", {"start": v(-33, -74.25) * mm, "end": v(-15, -92.25) * mm});
            skLineSegment(sketch, "E88.MirrorCS", {"start": v(-15, -92.25) * mm, "end": v(-15, -104.3) * mm});
            skArc(sketch, "E89.MirrorCS", {"start": v(15, -104.3) * mm, "mid": v(0, -119.25) * mm, "end": v(-15, -104.3) * mm});
            skCircle(sketch, "E90.MirrorC", {"center": v(0, -104.25) * mm, "radius": 6 * mm});
            skLineSegment(sketch, "E91.MirrorCS", {"start": v(15, -104.3) * mm, "end": v(15, -92.25) * mm});
            skLineSegment(sketch, "E92.MirrorCS", {"start": v(15, -92.25) * mm, "end": v(33, -74.25) * mm});
            skSolve(sketch);
        }
        {
            var Q0;
            {var subQ0=sQuery(id+"F16.wireOp",EDGE,"E87.MirrorCS");Q0=makeQuery(id+"F16.imprint","IMPRINT",FACE,{"disambiguationData":[TD([[makeQuery(id+"F16.imprint","IMPRINT",EDGE,{"derivedFrom":subQ0}),1.0]])]});}
            var Q1;
            Q1=makeQuery(id+"F16.imprint","IMPRINT",FACE,{"disambiguationData":[TD([[makeQuery(id+"F16.imprint","IMPRINT",EDGE,{"derivedFrom":makeQuery(id+"F1.opExtrude","CAP_EDGE",EDGE,{"disambiguationData":[OSD([sQuery(id+"F0.wireOp",EDGE,"E1.left")])],"isStart":true})}),-1.0]])]});
            var Q2;
            Q2=makeQuery(id+"F16.imprint","IMPRINT",FACE,{"disambiguationData":[TD([[makeQuery(id+"F16.imprint","IMPRINT",EDGE,{"derivedFrom":sQuery(id+"F16.wireOp",EDGE,"E80")}),-1.0]])]});
            var Q3;
            Q3=makeQuery(id+"F2.opExtrude","CAP_FACE",FACE,{"disambiguationData":[OSD([sQuery(id+"F0.wireOp",EDGE,"E12"),sQuery(id+"F0.wireOp",EDGE,"E13"),sQuery(id+"F0.wireOp",EDGE,"E14"),sQuery(id+"F0.wireOp",EDGE,"E15"),sQuery(id+"F0.wireOp",EDGE,"E17.filletArc"),sQuery(id+"F0.wireOp",EDGE,"E18.filletArc"),sQuery(id+"F0.wireOp",EDGE,"E19.filletArc"),sQuery(id+"F0.wireOp",EDGE,"E20.filletArc"),sQuery(id+"F0.wireOp",EDGE,"E25.0"),sQuery(id+"F0.wireOp",EDGE,"E25.1"),sQuery(id+"F0.wireOp",EDGE,"E25.2"),sQuery(id+"F0.wireOp",EDGE,"E25.3"),sQuery(id+"F0.wireOp",EDGE,"E25.4"),sQuery(id+"F0.wireOp",EDGE,"E25.5"),sQuery(id+"F0.wireOp",EDGE,"E25.6"),sQuery(id+"F0.wireOp",EDGE,"E25.7")])],"isStart":false});
            extrude(context, id + "F17", {"entities" : qUnion([Q0, Q1, Q2]), "operationType" : NewBodyOperationType.ADD, "endBound" : BoundingType.UP_TO_SURFACE, "endBoundEntityFace" : qUnion([Q3]), "depth" : 25 * mm});
        }
    });
